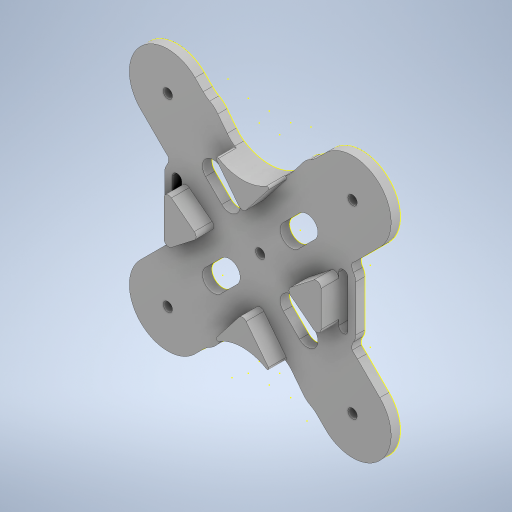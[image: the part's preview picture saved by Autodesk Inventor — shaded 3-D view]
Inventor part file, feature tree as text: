
AUTODESK INVENTOR PART (.ipt)
format: ipt  version: 2023 (Build 270158000, 158)  size: 442,368 bytes
history: native  units: in
note: dims shown in document units (in); Inventor stores cm internally (conversion verified against a paired STEP export)
features: sketch x1, projected_geometry x1, other x1
ambient origin geometry x8: Origin, YZ Plane, XZ Plane, XY Plane, X Axis, Y Axis, Z Axis, Center Point
bodies: Solid2 (feature_tree)
feature tree (3):
  sketch  "Sketch1"
  projected_geometry  "Projected Loop1"
  other  "Body169 (1) (1) (3)"
